# Revit family: Electronics_Messaging-Processors_Biamp_Vocia_Text-to-Speech-Engine_TTS-1__
name_source: partatom
category: Communication Devices
units: mm (PartAtom-declared; Revit-internal decimal feet)

## family parameters
Cut with Voids When Loaded = No
Host = Face
Maintain Annotation Orientation = No
OmniClass Number = 23.85.10.11.11
OmniClass Title = Sound and Signal Devices
Part Type = Normal
Room Calculation Point = No
Round Connector Dimension = Use Diameter
Shared = No

## types (2) — shared parameters
Altitude = 0-10,000 f (0-3000m) MSL
Apparent Load = 300 VA
Compliance = FCC Part 15 Class A (USA), CE marked (Europe), UL listed (USA and Canada), RoHS Directive (Europe)
Connector Description = 100-240VAC 50/60Hz
Default Elevation = 48 "
Depth = 17.5 "
Height = 1.75 "
Housing Material = Biamp - Metal - Black
Humidity = 5-95% non-condensing
Manufacturer = Biamp
Max Power Consumption = 300 W
Network Connection = RJ-45 with shielded Ethernet (CAT5, CAT5e, CAT6, or CAT7)
Number of Poles = 1
Power Factor = 1
Product Documentation Link = https://downloads.biamp.com
Product Page URL = https://www.biamp.com
Product data url = https://www.bimobject.com
Temperature Range = 32 - 113° F (0 – 45° C)
URL = https://www.biamp.com
Voltage = 120 V
Weight = 12.00 lbf
Width = 19 "

## per-type parameters (varying)
| type | Description | Model |
| TTS-1e | Vocia® TTS-1e Text-to-Speech Engine | Vocia TTS-1e |
| TTS-1nce | Vocia® TTS-1nce Text-to-Speech Engine | Vocia TTS-1nce |

## geometry (parser evidence)
native form markers: Sweep x2
no freeform markers — native parametric forms only
